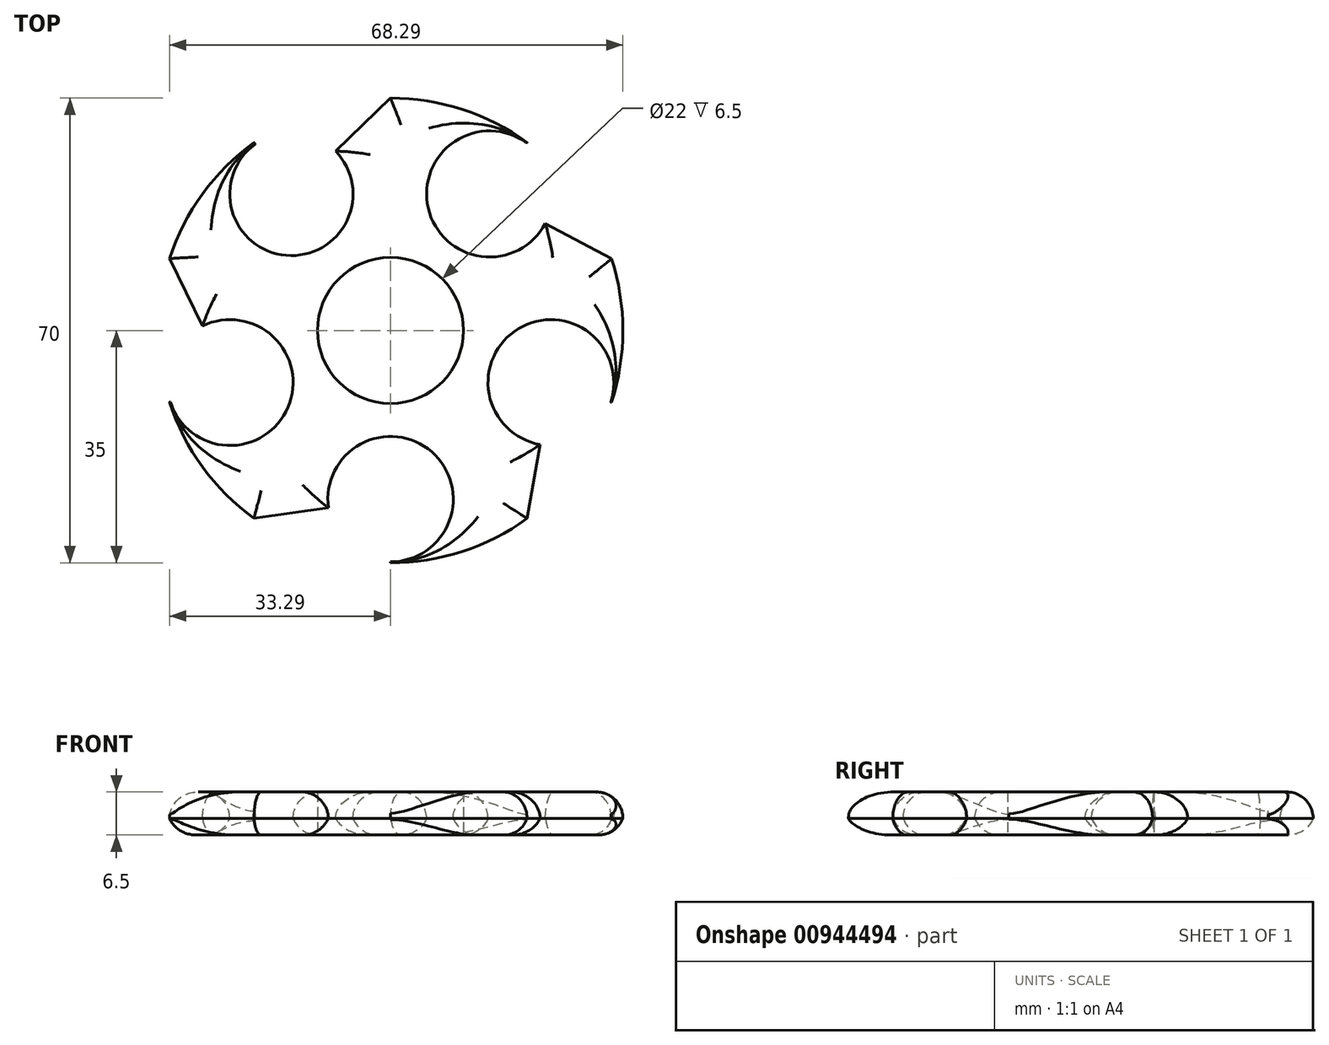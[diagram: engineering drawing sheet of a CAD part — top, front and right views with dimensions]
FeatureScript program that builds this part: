
annotation { "Feature Type Name" : "Feature", "Feature Type Description" : "" }
export const myFeature = defineFeature(function(context is Context, id is Id, definition is map)
    precondition{}
    {
        {
            var Q0;
            Q0=qCreatedBy(makeId("Top.planeOp"),FACE);
            var sketch = newSketch(context, id + "F0", { "sketchPlane" : qUnion([Q0])});
            skCircle(sketch, "E0", {"center": v(0, 0) * mm, "radius": 11 * mm});
            skCircle(sketch, "E1", {"center": v(0, 0) * mm, "radius": 35 * mm});
            skCircle(sketch, "E2.cCircle", {"center": v(0, 0) * mm, "radius": 41.1 * mm, "construction": true});
            skLineSegment(sketch, "E2.0", {"start": v(-29.87, 41.1) * mm, "end": v(29.87, 41.1) * mm});
            skLineSegment(sketch, "E2.1", {"start": v(29.87, 41.1) * mm, "end": v(48.33, -15.7) * mm});
            skLineSegment(sketch, "E2.2", {"start": v(48.33, -15.7) * mm, "end": v(0, -50.81) * mm});
            skLineSegment(sketch, "E2.3", {"start": v(0, -50.81) * mm, "end": v(-48.33, -15.7) * mm});
            skLineSegment(sketch, "E2.4", {"start": v(-48.33, -15.7) * mm, "end": v(-29.87, 41.1) * mm});
            skPoint(sketch, "E2.0.midPoint", {"position": v(0, 41.1) * mm});
            skLineSegment(sketch, "E3", {"start": v(-24.16, -33.26) * mm, "end": v(0, 0) * mm});
            skLineSegment(sketch, "E4", {"start": v(24.16, -33.26) * mm, "end": v(0, 0) * mm});
            skLineSegment(sketch, "E5", {"start": v(39.1, 12.7) * mm, "end": v(0, 0) * mm});
            skLineSegment(sketch, "E6", {"start": v(0, 41.1) * mm, "end": v(0, 0) * mm});
            skLineSegment(sketch, "E7", {"start": v(-39.1, 12.7) * mm, "end": v(0, 0) * mm});
            skLineSegment(sketch, "E8", {"start": v(29.87, 41.1) * mm, "end": v(0, 0) * mm});
            skLineSegment(sketch, "E9", {"start": v(-29.87, 41.1) * mm, "end": v(0, 0) * mm});
            skLineSegment(sketch, "E10", {"start": v(-48.33, -15.7) * mm, "end": v(0, 0) * mm});
            skLineSegment(sketch, "E11", {"start": v(0, -50.81) * mm, "end": v(0, 0) * mm});
            skLineSegment(sketch, "E12", {"start": v(48.33, -15.7) * mm, "end": v(0, 0) * mm});
            skCircle(sketch, "E13", {"center": v(14.93, 20.55) * mm, "radius": 9.5 * mm});
            skCircle(sketch, "E14", {"center": v(-14.93, 20.55) * mm, "radius": 9.28 * mm});
            skCircle(sketch, "E15", {"center": v(-24.16, -7.85) * mm, "radius": 9.48 * mm});
            skCircle(sketch, "E16", {"center": v(0, -25.4) * mm, "radius": 9.45 * mm});
            skCircle(sketch, "E17", {"center": v(24.16, -7.85) * mm, "radius": 9.47 * mm});
            skLineSegment(sketch, "E18", {"start": v(-14.93, 20.55) * mm, "end": v(0, 35) * mm});
            skLineSegment(sketch, "E19", {"start": v(14.93, 20.55) * mm, "end": v(33.29, 10.82) * mm});
            skLineSegment(sketch, "E20", {"start": v(24.16, -7.85) * mm, "end": v(20.57, -28.32) * mm});
            skLineSegment(sketch, "E21", {"start": v(0, -25.4) * mm, "end": v(-20.57, -28.32) * mm});
            skLineSegment(sketch, "E22", {"start": v(-24.16, -7.85) * mm, "end": v(-33.29, 10.82) * mm});
            skSolve(sketch);
        }
        {
            var Q0;
            {var subQ5=sQuery(id+"F0.wireOp",EDGE,"E6");var subQ7=sQuery(id+"F0.wireOp",EDGE,"E0");var subQ9=makeQuery(id+"F0.imprint","INTERSECT",VERTEX,{"derivedFrom":[subQ7,subQ5]});Q0=makeQuery(id+"F0.imprint","IMPRINT",FACE,{"disambiguationData":[TD([[makeQuery(id+"F0.imprint","IMPRINT",EDGE,{"disambiguationData":[TD([[subQ9,-1.0]])],"derivedFrom":subQ7}),-1.0]])]});}
            var Q1;
            {var subQ3=sQuery(id+"F0.wireOp",EDGE,"E0");var subQ5=sQuery(id+"F0.wireOp",EDGE,"E8");var subQ9=makeQuery(id+"F0.imprint","INTERSECT",VERTEX,{"derivedFrom":[subQ3,subQ5]});Q1=makeQuery(id+"F0.imprint","IMPRINT",FACE,{"disambiguationData":[TD([[makeQuery(id+"F0.imprint","IMPRINT",EDGE,{"disambiguationData":[TD([[subQ9,-1.0]])],"derivedFrom":subQ3}),-1.0]])]});}
            var Q2;
            {var subQ1=sQuery(id+"F0.wireOp",EDGE,"E8");var subQ5=sQuery(id+"F0.wireOp",EDGE,"E0");var subQ6=makeQuery(id+"F0.imprint","INTERSECT",VERTEX,{"derivedFrom":[subQ5,subQ1]});Q2=makeQuery(id+"F0.imprint","IMPRINT",FACE,{"disambiguationData":[TD([[makeQuery(id+"F0.imprint","IMPRINT",EDGE,{"disambiguationData":[TD([[subQ6,1.0]])],"derivedFrom":subQ5}),-1.0]])]});}
            var Q3;
            {var subQ5=sQuery(id+"F0.wireOp",EDGE,"E5");var subQ7=sQuery(id+"F0.wireOp",EDGE,"E0");var subQ8=makeQuery(id+"F0.imprint","INTERSECT",VERTEX,{"derivedFrom":[subQ7,subQ5]});Q3=makeQuery(id+"F0.imprint","IMPRINT",FACE,{"disambiguationData":[TD([[makeQuery(id+"F0.imprint","IMPRINT",EDGE,{"disambiguationData":[TD([[subQ8,1.0]])],"derivedFrom":subQ7}),-1.0]])]});}
            var Q4;
            {var subQ5=sQuery(id+"F0.wireOp",EDGE,"E4");var subQ7=sQuery(id+"F0.wireOp",EDGE,"E0");var subQ8=makeQuery(id+"F0.imprint","INTERSECT",VERTEX,{"derivedFrom":[subQ7,subQ5]});Q4=makeQuery(id+"F0.imprint","IMPRINT",FACE,{"disambiguationData":[TD([[makeQuery(id+"F0.imprint","IMPRINT",EDGE,{"disambiguationData":[TD([[subQ8,-1.0]])],"derivedFrom":subQ7}),-1.0]])]});}
            var Q5;
            {var subQ0=sQuery(id+"F0.wireOp",EDGE,"E11");var subQ8=sQuery(id+"F0.wireOp",EDGE,"E0");var subQ10=makeQuery(id+"F0.imprint","INTERSECT",VERTEX,{"derivedFrom":[subQ8,subQ0]});Q5=makeQuery(id+"F0.imprint","IMPRINT",FACE,{"disambiguationData":[TD([[makeQuery(id+"F0.imprint","IMPRINT",EDGE,{"disambiguationData":[TD([[subQ10,-1.0]])],"derivedFrom":subQ8}),-1.0]])]});}
            var Q6;
            {var subQ5=sQuery(id+"F0.wireOp",EDGE,"E0");var subQ7=sQuery(id+"F0.wireOp",EDGE,"E3");var subQ9=makeQuery(id+"F0.imprint","INTERSECT",VERTEX,{"derivedFrom":[subQ5,subQ7]});Q6=makeQuery(id+"F0.imprint","IMPRINT",FACE,{"disambiguationData":[TD([[makeQuery(id+"F0.imprint","IMPRINT",EDGE,{"disambiguationData":[TD([[subQ9,-1.0]])],"derivedFrom":subQ5}),-1.0]])]});}
            var Q7;
            {var subQ0=sQuery(id+"F0.wireOp",EDGE,"E10");var subQ7=sQuery(id+"F0.wireOp",EDGE,"E0");var subQ9=makeQuery(id+"F0.imprint","INTERSECT",VERTEX,{"derivedFrom":[subQ7,subQ0]});Q7=makeQuery(id+"F0.imprint","IMPRINT",FACE,{"disambiguationData":[TD([[makeQuery(id+"F0.imprint","IMPRINT",EDGE,{"disambiguationData":[TD([[subQ9,-1.0]])],"derivedFrom":subQ7}),-1.0]])]});}
            var Q8;
            {var subQ5=sQuery(id+"F0.wireOp",EDGE,"E7");var subQ6=sQuery(id+"F0.wireOp",EDGE,"E0");var subQ7=makeQuery(id+"F0.imprint","INTERSECT",VERTEX,{"derivedFrom":[subQ6,subQ5]});Q8=makeQuery(id+"F0.imprint","IMPRINT",FACE,{"disambiguationData":[TD([[makeQuery(id+"F0.imprint","IMPRINT",EDGE,{"disambiguationData":[TD([[subQ7,-1.0]])],"derivedFrom":subQ6}),-1.0]])]});}
            var Q9;
            {var subQ0=sQuery(id+"F0.wireOp",EDGE,"E9");var subQ7=sQuery(id+"F0.wireOp",EDGE,"E0");var subQ10=makeQuery(id+"F0.imprint","INTERSECT",VERTEX,{"derivedFrom":[subQ7,subQ0]});Q9=makeQuery(id+"F0.imprint","IMPRINT",FACE,{"disambiguationData":[TD([[makeQuery(id+"F0.imprint","IMPRINT",EDGE,{"disambiguationData":[TD([[subQ10,-1.0]])],"derivedFrom":subQ7}),-1.0]])]});}
            extrude(context, id + "F1", {"entities" : qUnion([Q0, Q1, Q2, Q3, Q4, Q5, Q6, Q7, Q8, Q9]), "depth" : 6.5 * mm, "offsetDistance" : 25 * mm});
        }
        {
            var Q0;
            {var subQ0=sQuery(id+"F0.wireOp",EDGE,"E1");Q0=makeQuery(id+"F1.opExtrude","CAP_EDGE",EDGE,{"disambiguationData":[OSD([subQ0]),TDD([makeQuery(id+"F0.imprint","IMPRINT",EDGE,{"disambiguationData":[TD([[makeQuery(id+"F0.imprint","INTERSECT",VERTEX,{"derivedFrom":[subQ0,sQuery(id+"F0.wireOp",EDGE,"E9")]}),-1.0]])],"derivedFrom":subQ0})])],"isStart":false});}
            var Q1;
            Q1=makeQuery(id+"F1.opExtrude","CAP_EDGE",EDGE,{"disambiguationData":[OSD([sQuery(id+"F0.wireOp",EDGE,"E14")])],"isStart":false});
            var Q2;
            Q2=makeQuery(id+"F1.opExtrude","CAP_EDGE",EDGE,{"disambiguationData":[OSD([sQuery(id+"F0.wireOp",EDGE,"E18")])],"isStart":false});
            var Q3;
            {var subQ0=sQuery(id+"F0.wireOp",EDGE,"E1");Q3=makeQuery(id+"F1.opExtrude","CAP_EDGE",EDGE,{"disambiguationData":[OSD([subQ0]),TDD([makeQuery(id+"F0.imprint","IMPRINT",EDGE,{"disambiguationData":[TD([[makeQuery(id+"F0.imprint","INTERSECT",VERTEX,{"derivedFrom":[subQ0,sQuery(id+"F0.wireOp",EDGE,"E8")]}),-1.0]])],"derivedFrom":subQ0})])],"isStart":false});}
            var Q4;
            Q4=makeQuery(id+"F1.opExtrude","CAP_EDGE",EDGE,{"disambiguationData":[OSD([sQuery(id+"F0.wireOp",EDGE,"E13")])],"isStart":false});
            var Q5;
            Q5=makeQuery(id+"F1.opExtrude","CAP_EDGE",EDGE,{"disambiguationData":[OSD([sQuery(id+"F0.wireOp",EDGE,"E19")])],"isStart":false});
            var Q6;
            {var subQ0=sQuery(id+"F0.wireOp",EDGE,"E1");Q6=makeQuery(id+"F1.opExtrude","CAP_EDGE",EDGE,{"disambiguationData":[OSD([subQ0]),TDD([makeQuery(id+"F0.imprint","IMPRINT",EDGE,{"disambiguationData":[TD([[makeQuery(id+"F0.imprint","INTERSECT",VERTEX,{"derivedFrom":[subQ0,sQuery(id+"F0.wireOp",EDGE,"E12")]}),-1.0]])],"derivedFrom":subQ0})])],"isStart":false});}
            var Q7;
            Q7=makeQuery(id+"F1.opExtrude","CAP_EDGE",EDGE,{"disambiguationData":[OSD([sQuery(id+"F0.wireOp",EDGE,"E17")])],"isStart":false});
            var Q8;
            Q8=makeQuery(id+"F1.opExtrude","CAP_EDGE",EDGE,{"disambiguationData":[OSD([sQuery(id+"F0.wireOp",EDGE,"E20")])],"isStart":false});
            var Q9;
            {var subQ0=sQuery(id+"F0.wireOp",EDGE,"E1");Q9=makeQuery(id+"F1.opExtrude","CAP_EDGE",EDGE,{"disambiguationData":[OSD([subQ0]),TDD([makeQuery(id+"F0.imprint","IMPRINT",EDGE,{"disambiguationData":[TD([[makeQuery(id+"F0.imprint","INTERSECT",VERTEX,{"derivedFrom":[subQ0,sQuery(id+"F0.wireOp",EDGE,"E11")]}),-1.0]])],"derivedFrom":subQ0})])],"isStart":false});}
            var Q10;
            Q10=makeQuery(id+"F1.opExtrude","CAP_EDGE",EDGE,{"disambiguationData":[OSD([sQuery(id+"F0.wireOp",EDGE,"E16")])],"isStart":false});
            var Q11;
            Q11=makeQuery(id+"F1.opExtrude","CAP_EDGE",EDGE,{"disambiguationData":[OSD([sQuery(id+"F0.wireOp",EDGE,"E21")])],"isStart":false});
            var Q12;
            {var subQ0=sQuery(id+"F0.wireOp",EDGE,"E1");Q12=makeQuery(id+"F1.opExtrude","CAP_EDGE",EDGE,{"disambiguationData":[OSD([subQ0]),TDD([makeQuery(id+"F0.imprint","IMPRINT",EDGE,{"disambiguationData":[TD([[makeQuery(id+"F0.imprint","INTERSECT",VERTEX,{"derivedFrom":[subQ0,sQuery(id+"F0.wireOp",EDGE,"E10")]}),-1.0]])],"derivedFrom":subQ0})])],"isStart":false});}
            var Q13;
            Q13=makeQuery(id+"F1.opExtrude","CAP_EDGE",EDGE,{"disambiguationData":[OSD([sQuery(id+"F0.wireOp",EDGE,"E15")])],"isStart":false});
            var Q14;
            Q14=makeQuery(id+"F1.opExtrude","CAP_EDGE",EDGE,{"disambiguationData":[OSD([sQuery(id+"F0.wireOp",EDGE,"E22")])],"isStart":false});
            fillet(context, id + "F2", {"entities" : qUnion([Q0, Q1, Q2, Q3, Q4, Q5, Q6, Q7, Q8, Q9, Q10, Q11, Q12, Q13, Q14]), "radius" : 4 * mm, "tangentPropagation" : true, "allowEdgeOverflow" : false});
        }
        {
            var Q0;
            Q0=makeQuery(id+"F1.opExtrude","CAP_EDGE",EDGE,{"disambiguationData":[OSD([sQuery(id+"F0.wireOp",EDGE,"E21")])],"isStart":true});
            var Q1;
            {var subQ0=sQuery(id+"F0.wireOp",EDGE,"E1");Q1=makeQuery(id+"F1.opExtrude","CAP_EDGE",EDGE,{"disambiguationData":[OSD([subQ0]),TDD([makeQuery(id+"F0.imprint","IMPRINT",EDGE,{"disambiguationData":[TD([[makeQuery(id+"F0.imprint","INTERSECT",VERTEX,{"derivedFrom":[subQ0,sQuery(id+"F0.wireOp",EDGE,"E10")]}),-1.0]])],"derivedFrom":subQ0})])],"isStart":true});}
            var Q2;
            Q2=makeQuery(id+"F1.opExtrude","CAP_EDGE",EDGE,{"disambiguationData":[OSD([sQuery(id+"F0.wireOp",EDGE,"E15")])],"isStart":true});
            var Q3;
            Q3=makeQuery(id+"F1.opExtrude","CAP_EDGE",EDGE,{"disambiguationData":[OSD([sQuery(id+"F0.wireOp",EDGE,"E22")])],"isStart":true});
            var Q4;
            {var subQ0=sQuery(id+"F0.wireOp",EDGE,"E1");Q4=makeQuery(id+"F1.opExtrude","CAP_EDGE",EDGE,{"disambiguationData":[OSD([subQ0]),TDD([makeQuery(id+"F0.imprint","IMPRINT",EDGE,{"disambiguationData":[TD([[makeQuery(id+"F0.imprint","INTERSECT",VERTEX,{"derivedFrom":[subQ0,sQuery(id+"F0.wireOp",EDGE,"E9")]}),-1.0]])],"derivedFrom":subQ0})])],"isStart":true});}
            var Q5;
            Q5=makeQuery(id+"F1.opExtrude","CAP_EDGE",EDGE,{"disambiguationData":[OSD([sQuery(id+"F0.wireOp",EDGE,"E14")])],"isStart":true});
            var Q6;
            Q6=makeQuery(id+"F1.opExtrude","CAP_EDGE",EDGE,{"disambiguationData":[OSD([sQuery(id+"F0.wireOp",EDGE,"E18")])],"isStart":true});
            var Q7;
            {var subQ0=sQuery(id+"F0.wireOp",EDGE,"E1");Q7=makeQuery(id+"F1.opExtrude","CAP_EDGE",EDGE,{"disambiguationData":[OSD([subQ0]),TDD([makeQuery(id+"F0.imprint","IMPRINT",EDGE,{"disambiguationData":[TD([[makeQuery(id+"F0.imprint","INTERSECT",VERTEX,{"derivedFrom":[subQ0,sQuery(id+"F0.wireOp",EDGE,"E8")]}),-1.0]])],"derivedFrom":subQ0})])],"isStart":true});}
            var Q8;
            Q8=makeQuery(id+"F1.opExtrude","CAP_EDGE",EDGE,{"disambiguationData":[OSD([sQuery(id+"F0.wireOp",EDGE,"E13")])],"isStart":true});
            var Q9;
            Q9=makeQuery(id+"F1.opExtrude","CAP_EDGE",EDGE,{"disambiguationData":[OSD([sQuery(id+"F0.wireOp",EDGE,"E19")])],"isStart":true});
            var Q10;
            {var subQ0=sQuery(id+"F0.wireOp",EDGE,"E1");Q10=makeQuery(id+"F1.opExtrude","CAP_EDGE",EDGE,{"disambiguationData":[OSD([subQ0]),TDD([makeQuery(id+"F0.imprint","IMPRINT",EDGE,{"disambiguationData":[TD([[makeQuery(id+"F0.imprint","INTERSECT",VERTEX,{"derivedFrom":[subQ0,sQuery(id+"F0.wireOp",EDGE,"E12")]}),-1.0]])],"derivedFrom":subQ0})])],"isStart":true});}
            var Q11;
            Q11=makeQuery(id+"F1.opExtrude","CAP_EDGE",EDGE,{"disambiguationData":[OSD([sQuery(id+"F0.wireOp",EDGE,"E17")])],"isStart":true});
            var Q12;
            Q12=makeQuery(id+"F1.opExtrude","CAP_EDGE",EDGE,{"disambiguationData":[OSD([sQuery(id+"F0.wireOp",EDGE,"E20")])],"isStart":true});
            var Q13;
            {var subQ0=sQuery(id+"F0.wireOp",EDGE,"E1");Q13=makeQuery(id+"F1.opExtrude","CAP_EDGE",EDGE,{"disambiguationData":[OSD([subQ0]),TDD([makeQuery(id+"F0.imprint","IMPRINT",EDGE,{"disambiguationData":[TD([[makeQuery(id+"F0.imprint","INTERSECT",VERTEX,{"derivedFrom":[subQ0,sQuery(id+"F0.wireOp",EDGE,"E11")]}),-1.0]])],"derivedFrom":subQ0})])],"isStart":true});}
            var Q14;
            Q14=makeQuery(id+"F1.opExtrude","CAP_EDGE",EDGE,{"disambiguationData":[OSD([sQuery(id+"F0.wireOp",EDGE,"E16")])],"isStart":true});
            fillet(context, id + "F3", {"entities" : qUnion([Q0, Q1, Q2, Q3, Q4, Q5, Q6, Q7, Q8, Q9, Q10, Q11, Q12, Q13, Q14]), "radius" : 4 * mm, "tangentPropagation" : true, "allowEdgeOverflow" : false});
        }
    });
